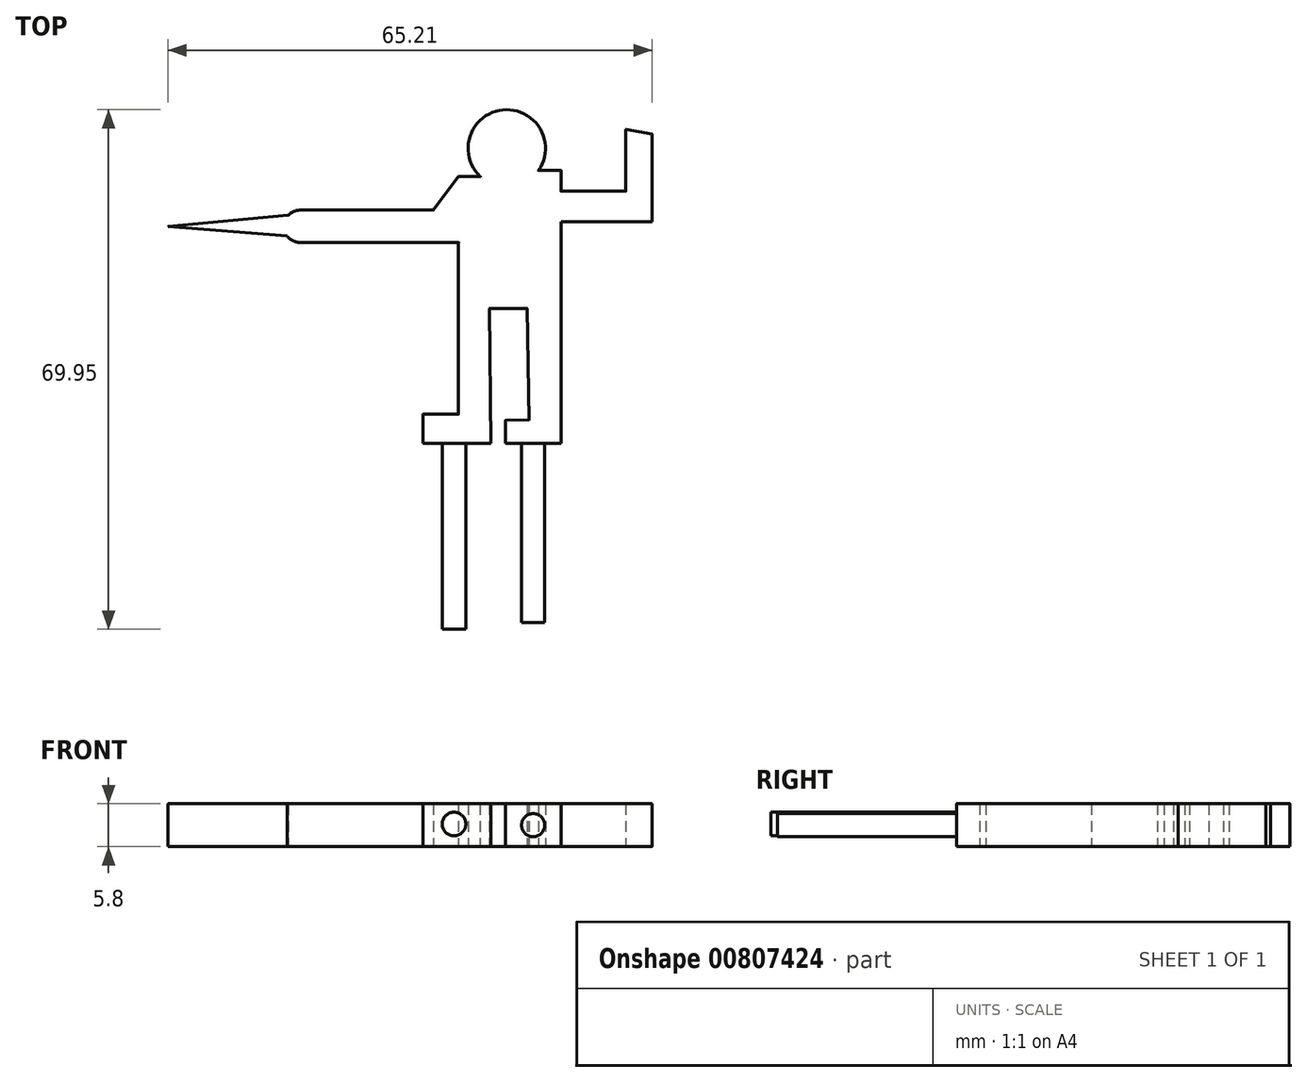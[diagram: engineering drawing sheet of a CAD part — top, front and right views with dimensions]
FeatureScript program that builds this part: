
annotation { "Feature Type Name" : "Feature", "Feature Type Description" : "" }
export const myFeature = defineFeature(function(context is Context, id is Id, definition is map)
    precondition{}
    {
        {
            var Q0;
            Q0=qCreatedBy(makeId("Top.planeOp"),FACE);
            var sketch = newSketch(context, id + "F0", { "sketchPlane" : qUnion([Q0])});
            skCircle(sketch, "E0", {"center": v(-23.03, 38.54) * mm, "radius": 5.22 * mm});
            skLineSegment(sketch, "E1", {"start": v(-26.6, 34.75) * mm, "end": v(-29.54, 34.75) * mm});
            skLineSegment(sketch, "E2", {"start": v(-29.54, 34.75) * mm, "end": v(-29.54, 17) * mm});
            skLineSegment(sketch, "E3", {"start": v(-15.71, 17) * mm, "end": v(-15.71, 35.57) * mm});
            skLineSegment(sketch, "E4", {"start": v(-15.71, 35.57) * mm, "end": v(-18.74, 35.57) * mm});
            skLineSegment(sketch, "E5", {"start": v(-15.71, 28.65) * mm, "end": v(-3.46, 28.65) * mm});
            skLineSegment(sketch, "E6", {"start": v(-3.46, 28.65) * mm, "end": v(-3.46, 40.51) * mm});
            skLineSegment(sketch, "E7", {"start": v(-3.46, 40.51) * mm, "end": v(-6.98, 41.1) * mm});
            skLineSegment(sketch, "E8", {"start": v(-6.98, 41.1) * mm, "end": v(-6.98, 32.8) * mm});
            skLineSegment(sketch, "E9", {"start": v(-6.98, 32.8) * mm, "end": v(-15.71, 32.8) * mm});
            skLineSegment(sketch, "E10", {"start": v(-29.54, 34.75) * mm, "end": v(-32.9, 30.24) * mm});
            skLineSegment(sketch, "E11", {"start": v(-32.9, 30.24) * mm, "end": v(-50.89, 30.24) * mm});
            skLineSegment(sketch, "E12", {"start": v(-50.89, 30.24) * mm, "end": v(-50.89, 25.89) * mm});
            skLineSegment(sketch, "E13", {"start": v(-50.89, 25.89) * mm, "end": v(-29.54, 25.89) * mm});
            skArc(sketch, "E14", {"start": v(-50.89, 30.24) * mm, "mid": v(-53.06, 28.06) * mm, "end": v(-50.89, 25.89) * mm});
            skLineSegment(sketch, "E15", {"start": v(-52.61, 26.74) * mm, "end": v(-68.67, 28.06) * mm});
            skPoint(sketch, "E15.endSnap0", {"position": v(-53.06, 28.06) * mm});
            skLineSegment(sketch, "E16", {"start": v(-52.46, 29.56) * mm, "end": v(-68.67, 28.06) * mm});
            skLineSegment(sketch, "E17", {"start": v(-25.4, 17) * mm, "end": v(-25.15, -1.19) * mm});
            skLineSegment(sketch, "E18", {"start": v(-25.15, -1.19) * mm, "end": v(-34.29, -1.19) * mm});
            skLineSegment(sketch, "E19", {"start": v(-34.29, -1.19) * mm, "end": v(-34.29, 2.77) * mm});
            skLineSegment(sketch, "E20", {"start": v(-34.29, 2.77) * mm, "end": v(-29.54, 2.77) * mm});
            skLineSegment(sketch, "E21", {"start": v(-29.54, 2.77) * mm, "end": v(-29.54, 17) * mm});
            skLineSegment(sketch, "E22", {"start": v(-15.71, 17) * mm, "end": v(-15.71, -1.19) * mm});
            skLineSegment(sketch, "E23", {"start": v(-20.06, 1.98) * mm, "end": v(-20.26, 17) * mm});
            skLineSegment(sketch, "E24", {"start": v(-20.06, 1.98) * mm, "end": v(-23.23, 1.93) * mm});
            skLineSegment(sketch, "E25", {"start": v(-23.23, 1.93) * mm, "end": v(-23.23, -1.19) * mm});
            skLineSegment(sketch, "E26", {"start": v(-23.23, -1.19) * mm, "end": v(-15.71, -1.19) * mm});
            skLineSegment(sketch, "E27", {"start": v(-29.54, 17) * mm, "end": v(-15.71, 17) * mm});
            skSolve(sketch);
        }
        {
            var Q0;
            Q0 = qSketchRegion(id + "F0", true);
            extrude(context, id + "F1", {"entities" : qUnion([Q0]), "depth" : 5.8 * mm, "offsetDistance" : 25 * mm});
        }
        {
            var Q0;
            Q0=makeQuery(id+"F1.opExtrude","SWEPT_FACE",FACE,{"disambiguationData":[OSD([sQuery(id+"F0.wireOp",EDGE,"E18")])]});
            var sketch = newSketch(context, id + "F2", { "sketchPlane" : qUnion([Q0])});
            skCircle(sketch, "E28", {"center": v(-30.14, 3.05) * mm, "radius": 1.6 * mm});
            skCircle(sketch, "E29", {"center": v(-9.43, 3.05) * mm, "radius": 1.52 * mm});
            skSolve(sketch);
        }
        {
            var Q0;
            Q0=makeQuery(id+"F2.imprint","IMPRINT",FACE,{"disambiguationData":[TD([[makeQuery(id+"F2.imprint","IMPRINT",EDGE,{"derivedFrom":sQuery(id+"F2.wireOp",EDGE,"E28")}),1.0]])]});
            extrude(context, id + "F3", {"entities" : qUnion([Q0]), "operationType" : NewBodyOperationType.ADD, "depth" : 25 * mm, "offsetDistance" : 25 * mm});
        }
        {
            var Q0;
            Q0=makeQuery(id+"F1.opExtrude","SWEPT_FACE",FACE,{"disambiguationData":[OSD([sQuery(id+"F0.wireOp",EDGE,"E26")])]});
            var sketch = newSketch(context, id + "F4", { "sketchPlane" : qUnion([Q0])});
            skCircle(sketch, "E30", {"center": v(-19.47, 2.9) * mm, "radius": 1.56 * mm});
            skPoint(sketch, "E30.centerSnap0", {"position": v(-19.47, 0) * mm});
            skPoint(sketch, "E30.centerSnap1", {"position": v(-15.71, 2.9) * mm});
            skSolve(sketch);
        }
        {
            var Q0;
            Q0 = qSketchRegion(id + "F4", true);
            extrude(context, id + "F5", {"entities" : qUnion([Q0]), "operationType" : NewBodyOperationType.ADD, "depth" : 24.1 * mm, "offsetDistance" : 25 * mm});
        }
        {
            var Q0;
            Q0=makeQuery(id+"F1.opExtrude","CAP_EDGE",EDGE,{"disambiguationData":[OSD([sQuery(id+"F0.wireOp",EDGE,"E3"),sQuery(id+"F0.wireOp",EDGE,"E22")])],"isStart":false});
            var Q1;
            Q1=makeQuery(id+"F1.opExtrude","CAP_EDGE",EDGE,{"disambiguationData":[OSD([sQuery(id+"F0.wireOp",EDGE,"E5")])],"isStart":false});
            var Q2;
            Q2=makeQuery(id+"F1.opExtrude","CAP_EDGE",EDGE,{"disambiguationData":[OSD([sQuery(id+"F0.wireOp",EDGE,"E6")])],"isStart":false});
            var Q3;
            Q3=makeQuery(id+"F1.opExtrude","CAP_EDGE",EDGE,{"disambiguationData":[OSD([sQuery(id+"F0.wireOp",EDGE,"E6")])],"isStart":true});
            var Q4;
            Q4=makeQuery(id+"F1.opExtrude","CAP_FACE",FACE,{"disambiguationData":[OSD([sQuery(id+"F0.wireOp",EDGE,"E0"),sQuery(id+"F0.wireOp",EDGE,"E1"),sQuery(id+"F0.wireOp",EDGE,"E2"),sQuery(id+"F0.wireOp",EDGE,"E3"),sQuery(id+"F0.wireOp",EDGE,"E4"),sQuery(id+"F0.wireOp",EDGE,"E5"),sQuery(id+"F0.wireOp",EDGE,"E6"),sQuery(id+"F0.wireOp",EDGE,"E7"),sQuery(id+"F0.wireOp",EDGE,"E8"),sQuery(id+"F0.wireOp",EDGE,"E9"),sQuery(id+"F0.wireOp",EDGE,"E10"),sQuery(id+"F0.wireOp",EDGE,"E11"),sQuery(id+"F0.wireOp",EDGE,"E13"),sQuery(id+"F0.wireOp",EDGE,"E14"),sQuery(id+"F0.wireOp",EDGE,"E15"),sQuery(id+"F0.wireOp",EDGE,"E16"),sQuery(id+"F0.wireOp",EDGE,"E17"),sQuery(id+"F0.wireOp",EDGE,"E18"),sQuery(id+"F0.wireOp",EDGE,"E19"),sQuery(id+"F0.wireOp",EDGE,"E20"),sQuery(id+"F0.wireOp",EDGE,"E21"),sQuery(id+"F0.wireOp",EDGE,"E22"),sQuery(id+"F0.wireOp",EDGE,"E23"),sQuery(id+"F0.wireOp",EDGE,"E24"),sQuery(id+"F0.wireOp",EDGE,"E25"),sQuery(id+"F0.wireOp",EDGE,"E26"),sQuery(id+"F0.wireOp",EDGE,"E27")])],"isStart":false});
            fillet(context, id + "F6", {"entities" : qUnion([Q0, Q1, Q2, Q3, Q4]), "radius" : 0.02 * mm, "tangentPropagation" : true, "allowEdgeOverflow" : false});
        }
    });
